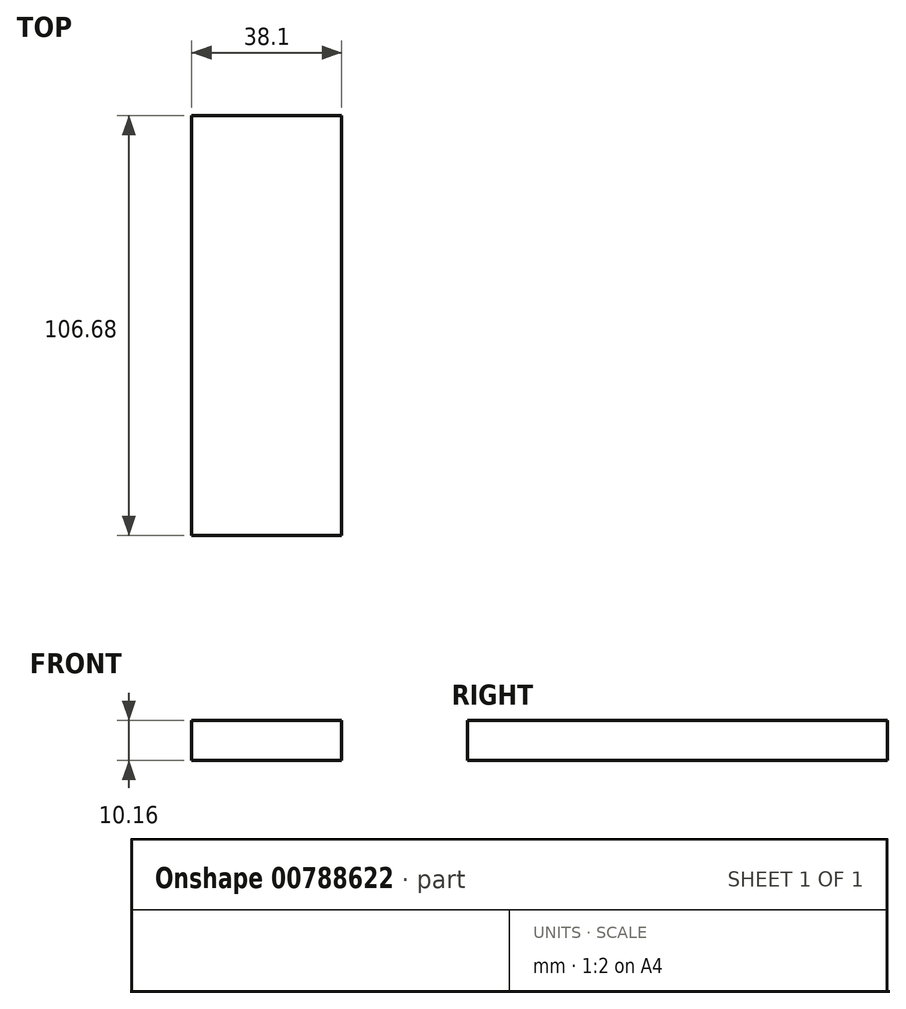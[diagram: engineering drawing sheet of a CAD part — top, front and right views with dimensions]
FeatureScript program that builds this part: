
annotation { "Feature Type Name" : "Feature", "Feature Type Description" : "" }
export const myFeature = defineFeature(function(context is Context, id is Id, definition is map)
    precondition{}
    {
        {
            var Q0;
            Q0=qCreatedBy(makeId("Top.planeOp"),FACE);
            var sketch = newSketch(context, id + "F0", { "sketchPlane" : qUnion([Q0])});
            skLineSegment(sketch, "E0.bottom", {"start": v(0, 0) * mm, "end": v(38.1, 0) * mm});
            skLineSegment(sketch, "E0.top", {"start": v(0, 106.68) * mm, "end": v(38.1, 106.68) * mm});
            skLineSegment(sketch, "E0.left", {"start": v(0, 0) * mm, "end": v(0, 106.68) * mm});
            skLineSegment(sketch, "E0.right", {"start": v(38.1, 0) * mm, "end": v(38.1, 106.68) * mm});
            skSolve(sketch);
        }
        {
            var Q0;
            Q0=qSketchRegion(id+"F0",true);
            extrude(context, id + "F1", {"entities" : qUnion([Q0]), "depth" : 10.16 * mm, "offsetDistance" : 25.4 * mm});
        }
    });
